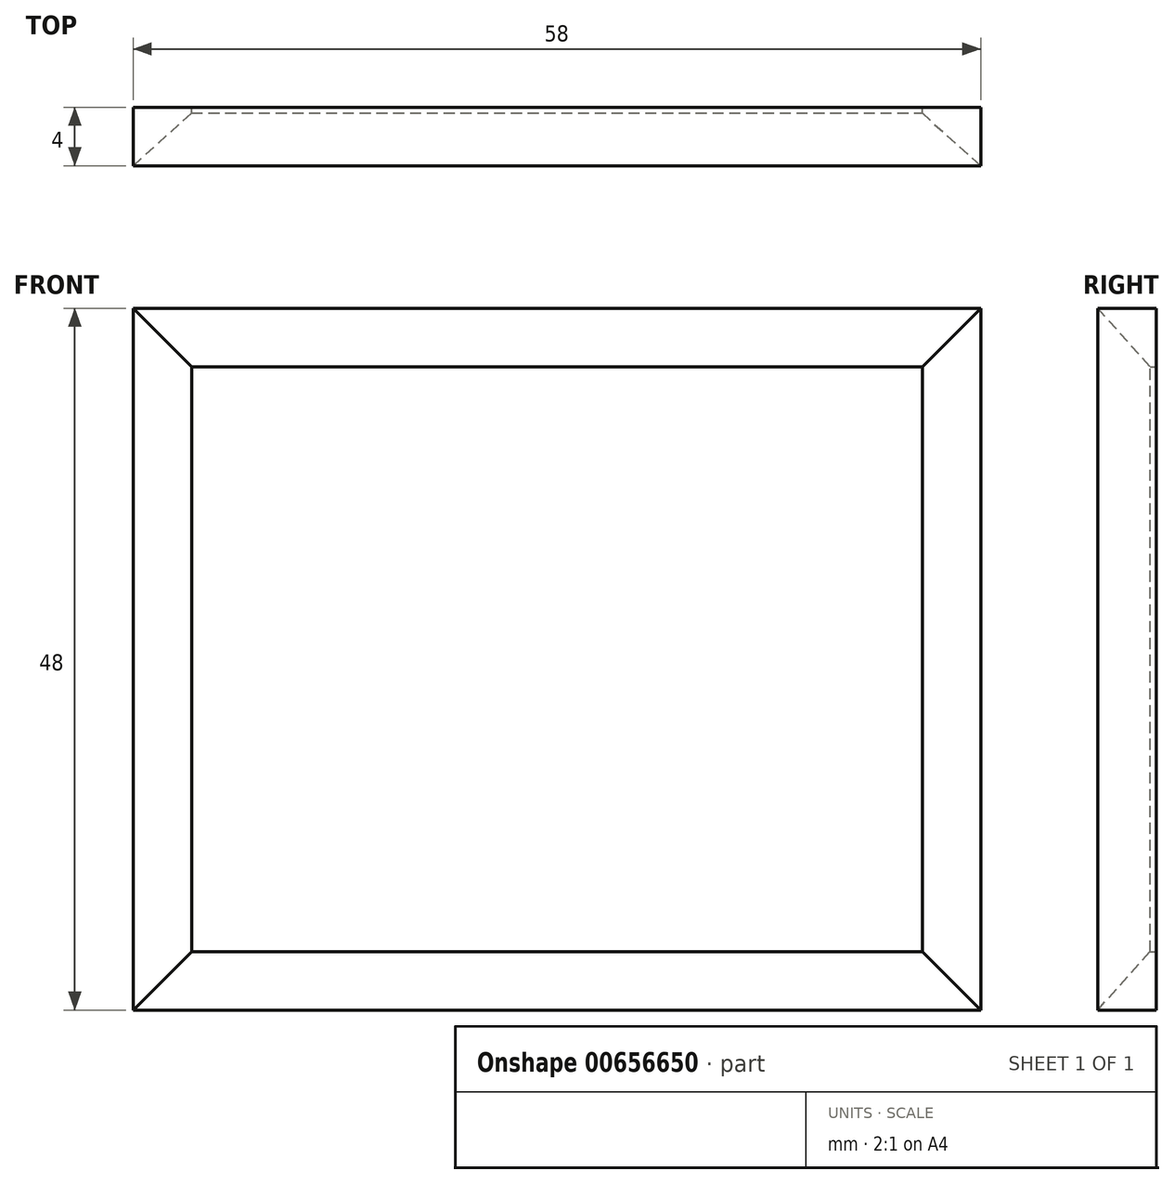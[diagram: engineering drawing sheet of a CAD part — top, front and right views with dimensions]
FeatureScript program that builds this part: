
annotation { "Feature Type Name" : "Feature", "Feature Type Description" : "" }
export const myFeature = defineFeature(function(context is Context, id is Id, definition is map)
    precondition{}
    {
        {
            assignVariable(context, id + "F0", {"name" : "ram", "anyValue" : 4});
        }
        {
            var Q0;
            Q0=qCreatedBy(makeId("Front.planeOp"),FACE);
            var sketch = newSketch(context, id + "F1", { "sketchPlane" : qUnion([Q0])});
            skLineSegment(sketch, "E0.bottom", {"start": v(25, -20) * mm, "end": v(-25, -20) * mm});
            skLineSegment(sketch, "E0.top", {"start": v(25, 20) * mm, "end": v(-25, 20) * mm});
            skLineSegment(sketch, "E0.left", {"start": v(25, -20) * mm, "end": v(25, 20) * mm});
            skLineSegment(sketch, "E0.right", {"start": v(-25, -20) * mm, "end": v(-25, 20) * mm});
            skPoint(sketch, "E0.middle", {"position": v(0, 0) * mm});
            skLineSegment(sketch, "E1.0", {"start": v(29, 24) * mm, "end": v(-29, 24) * mm});
            skLineSegment(sketch, "E1.1", {"start": v(29, -24) * mm, "end": v(29, 24) * mm});
            skLineSegment(sketch, "E1.2", {"start": v(29, -24) * mm, "end": v(-29, -24) * mm});
            skLineSegment(sketch, "E1.3", {"start": v(-29, -24) * mm, "end": v(-29, 24) * mm});
            skSolve(sketch);
        }
        {
            var Q0;
            Q0=makeQuery(id+"F1.imprint","IMPRINT",FACE,{"disambiguationData":[TD([[makeQuery(id+"F1.imprint","IMPRINT",EDGE,{"derivedFrom":sQuery(id+"F1.wireOp",EDGE,"E0.bottom")}),1.0]])]});
            extrude(context, id + "F2", {"entities" : qUnion([Q0]), "depth" : (getVariable(context, 'ram')) * mm, "offsetDistance" : 25 * mm});
        }
        {
            var Q0;
            Q0=makeQuery(id+"F2.opExtrude","CAP_EDGE",EDGE,{"disambiguationData":[OSD([sQuery(id+"F1.wireOp",EDGE,"E0.right")])],"isStart":false});
            var Q1;
            Q1=makeQuery(id+"F2.opExtrude","CAP_EDGE",EDGE,{"disambiguationData":[OSD([sQuery(id+"F1.wireOp",EDGE,"E0.top")])],"isStart":false});
            var Q2;
            Q2=makeQuery(id+"F2.opExtrude","CAP_EDGE",EDGE,{"disambiguationData":[OSD([sQuery(id+"F1.wireOp",EDGE,"E0.left")])],"isStart":false});
            var Q3;
            Q3=makeQuery(id+"F2.opExtrude","CAP_EDGE",EDGE,{"disambiguationData":[OSD([sQuery(id+"F1.wireOp",EDGE,"E0.bottom")])],"isStart":false});
            chamfer(context, id + "F3", {"entities" : qUnion([Q0, Q1, Q2, Q3]), "chamferType" : ChamferType.TWO_OFFSETS, "width1" : (getVariable(context, 'ram')) * mm, "oppositeDirection" : false, "width2" : (getVariable(context, 'ram') - 0.4) * mm, "tangentPropagation" : true});
        }
    });
